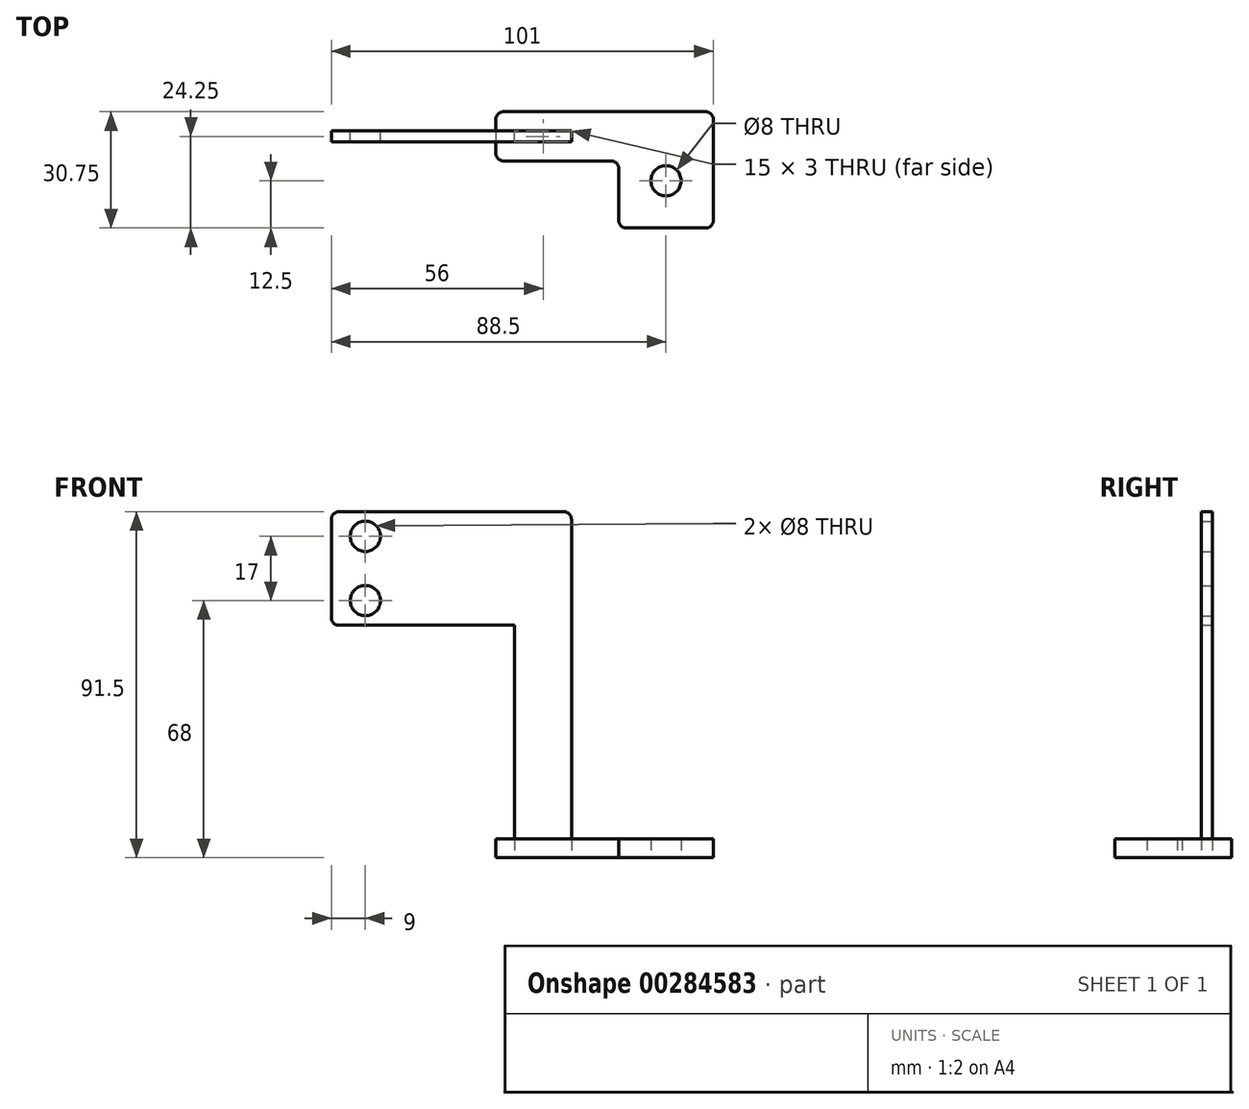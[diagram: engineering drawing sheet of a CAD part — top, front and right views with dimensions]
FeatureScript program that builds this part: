
annotation { "Feature Type Name" : "Feature", "Feature Type Description" : "" }
export const myFeature = defineFeature(function(context is Context, id is Id, definition is map)
    precondition{}
    {
        {
            var Q0;
            Q0=qCreatedBy(makeId("Top.planeOp"),FACE);
            var sketch = newSketch(context, id + "F0", { "sketchPlane" : qUnion([Q0])});
            skLineSegment(sketch, "E0.top", {"start": v(97.5, -25) * mm, "end": v(118.5, -25) * mm});
            skLineSegment(sketch, "E0.left", {"start": v(95.5, -9.25) * mm, "end": v(95.5, -23) * mm});
            skLineSegment(sketch, "E0.right", {"start": v(120.5, -7.25) * mm, "end": v(120.5, -23) * mm});
            skCircle(sketch, "E1", {"center": v(108, -12.5) * mm, "radius": 4 * mm});
            skPoint(sketch, "E2.visualSharp", {"position": v(95.5, -25) * mm});
            skArc(sketch, "E2.filletArc", {"start": v(95.5, -23) * mm, "mid": v(96.09, -24.41) * mm, "end": v(97.5, -25) * mm});
            skPoint(sketch, "E3.visualSharp", {"position": v(120.5, -25) * mm});
            skArc(sketch, "E3.filletArc", {"start": v(118.5, -25) * mm, "mid": v(119.91, -24.41) * mm, "end": v(120.5, -23) * mm});
            skLineSegment(sketch, "E4.bottom", {"start": v(68, 0.75) * mm, "end": v(83, 0.75) * mm});
            skLineSegment(sketch, "E4.top", {"start": v(68, -2.25) * mm, "end": v(83, -2.25) * mm});
            skLineSegment(sketch, "E4.left", {"start": v(68, 0.75) * mm, "end": v(68, -2.25) * mm});
            skLineSegment(sketch, "E4.right", {"start": v(83, 0.75) * mm, "end": v(83, -2.25) * mm});
            skLineSegment(sketch, "E5.bottom", {"start": v(65, 5.75) * mm, "end": v(118.5, 5.75) * mm});
            skLineSegment(sketch, "E5.top", {"start": v(65, -7.25) * mm, "end": v(93.5, -7.25) * mm});
            skLineSegment(sketch, "E5.left", {"start": v(63, 3.75) * mm, "end": v(63, -5.25) * mm});
            skLineSegment(sketch, "E5.right", {"start": v(120.5, 3.75) * mm, "end": v(120.5, -7.25) * mm});
            skPoint(sketch, "E0.bottom.start.orphan", {"position": v(95.5, 0) * mm});
            skPoint(sketch, "E6.visualSharp", {"position": v(63, -7.25) * mm});
            skArc(sketch, "E6.filletArc", {"start": v(63, -5.25) * mm, "mid": v(63.59, -6.66) * mm, "end": v(65, -7.25) * mm});
            skPoint(sketch, "E7.visualSharp", {"position": v(63, 5.75) * mm});
            skArc(sketch, "E7.filletArc", {"start": v(65, 5.75) * mm, "mid": v(63.59, 5.16) * mm, "end": v(63, 3.75) * mm});
            skPoint(sketch, "E8.visualSharp", {"position": v(120.5, 5.75) * mm});
            skArc(sketch, "E8.filletArc", {"start": v(120.5, 3.75) * mm, "mid": v(119.91, 5.16) * mm, "end": v(118.5, 5.75) * mm});
            skPoint(sketch, "E9.visualSharp", {"position": v(95.5, -7.25) * mm});
            skArc(sketch, "E9.filletArc", {"start": v(95.5, -9.25) * mm, "mid": v(94.91, -7.84) * mm, "end": v(93.5, -7.25) * mm});
            skSolve(sketch);
        }
        {
            var Q0;
            Q0=qSketchRegion(id+"F0",true);
            extrude(context, id + "F1", {"entities" : qUnion([Q0]), "depth" : 5 * mm});
        }
        {
            var Q0;
            Q0=makeQuery(id+"F1.opExtrude","SWEPT_FACE",FACE,{"disambiguationData":[OSD([sQuery(id+"F0.wireOp",EDGE,"E4.bottom")])]});
            var sketch = newSketch(context, id + "F2", { "sketchPlane" : qUnion([Q0])});
            skLineSegment(sketch, "E10.bottom", {"start": v(68, 0) * mm, "end": v(83, 0) * mm});
            skLineSegment(sketch, "E10.top", {"start": v(53, 91.5) * mm, "end": v(81, 91.5) * mm});
            skLineSegment(sketch, "E10.right", {"start": v(83, 0) * mm, "end": v(83, 89.5) * mm});
            skLineSegment(sketch, "E11.bottom", {"start": v(53, 91.5) * mm, "end": v(21.5, 91.5) * mm});
            skLineSegment(sketch, "E11.top", {"start": v(68, 61.5) * mm, "end": v(21.5, 61.5) * mm});
            skLineSegment(sketch, "E12", {"start": v(35, 91.5) * mm, "end": v(35, 61.5) * mm, "construction": true});
            skPoint(sketch, "E12.endSnap0", {"position": v(26.5, 61.5) * mm});
            skCircle(sketch, "E13", {"center": v(28.5, 85) * mm, "radius": 4 * mm});
            skCircle(sketch, "E14", {"center": v(28.5, 68) * mm, "radius": 4 * mm});
            skLineSegment(sketch, "E15", {"start": v(19.5, 89.5) * mm, "end": v(19.5, 63.5) * mm});
            skPoint(sketch, "E16.orphan", {"position": v(0, 61.5) * mm});
            skPoint(sketch, "E17.visualSharp", {"position": v(19.5, 61.5) * mm});
            skArc(sketch, "E17.filletArc", {"start": v(19.5, 63.5) * mm, "mid": v(20.09, 62.09) * mm, "end": v(21.5, 61.5) * mm});
            skPoint(sketch, "E18.visualSharp", {"position": v(83, 91.5) * mm});
            skArc(sketch, "E18.filletArc", {"start": v(83, 89.5) * mm, "mid": v(82.41, 90.91) * mm, "end": v(81, 91.5) * mm});
            skPoint(sketch, "E19.visualSharp", {"position": v(19.5, 91.5) * mm});
            skArc(sketch, "E19.filletArc", {"start": v(21.5, 91.5) * mm, "mid": v(20.09, 90.91) * mm, "end": v(19.5, 89.5) * mm});
            skPoint(sketch, "E20", {"position": v(0, 76.5) * mm});
            skPoint(sketch, "E21", {"position": v(-40, 89) * mm});
            skLineSegment(sketch, "E22", {"start": v(28.5, 85) * mm, "end": v(28.5, 68) * mm, "construction": true});
            skLineSegment(sketch, "E23", {"start": v(28.5, 76.5) * mm, "end": v(0, 76.5) * mm, "construction": true});
            skLineSegment(sketch, "E24", {"start": v(68, 61.5) * mm, "end": v(68, 0) * mm});
            skPoint(sketch, "E25.orphan", {"position": v(51, 61.5) * mm});
            skSolve(sketch);
        }
        {
            var Q0;
            Q0=qSketchRegion(id+"F2",true);
            extrude(context, id + "F3", {"entities" : qUnion([Q0]), "depth" : 3 * mm});
        }
    });
